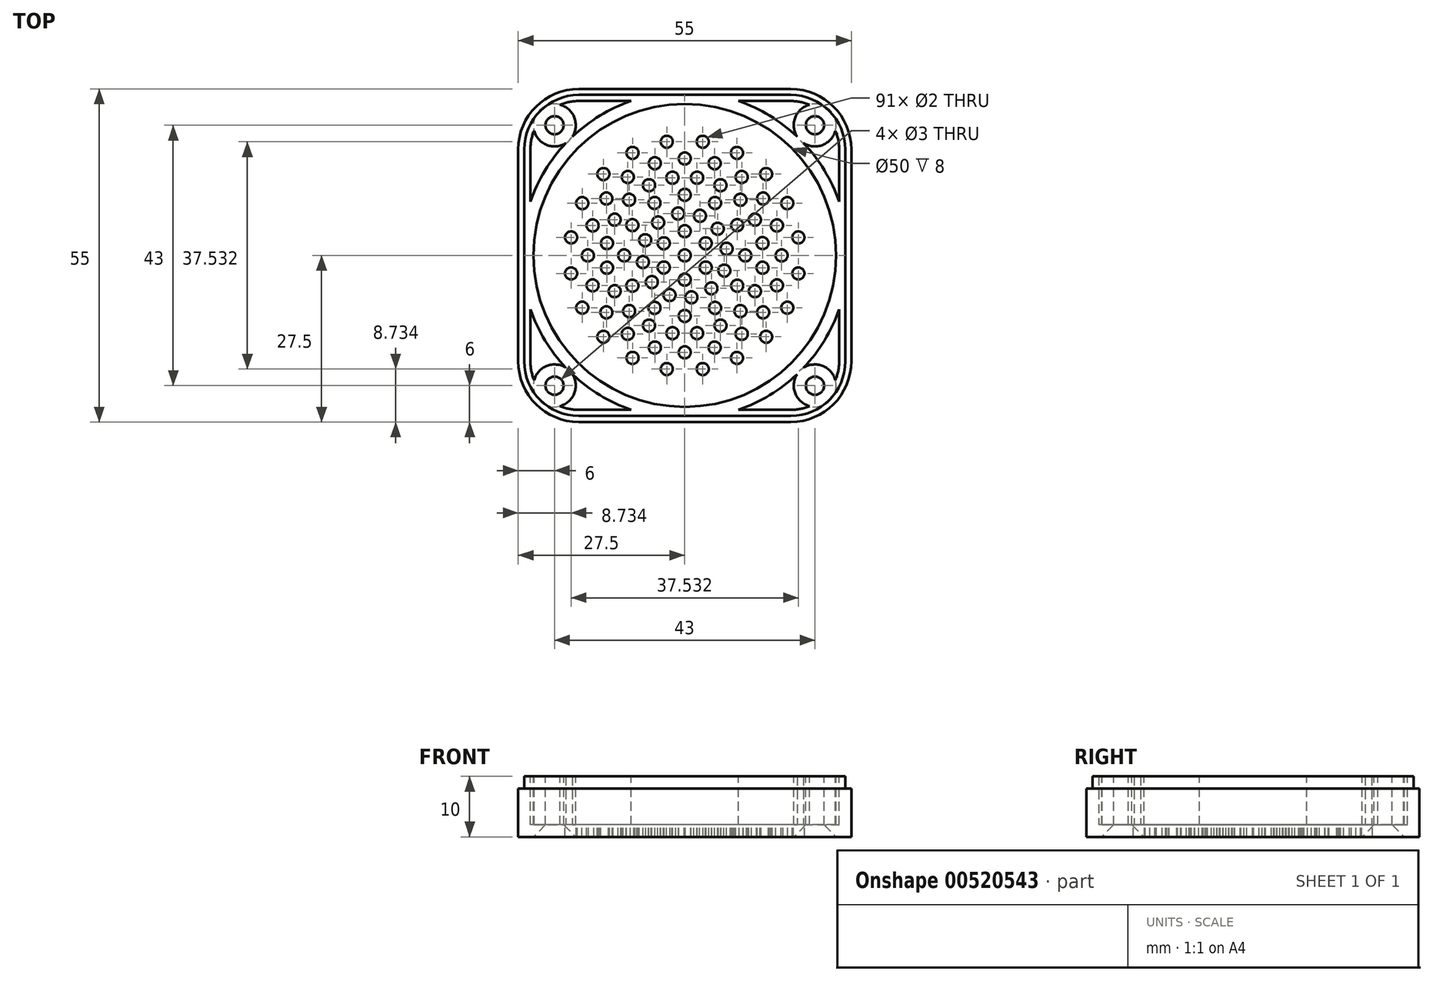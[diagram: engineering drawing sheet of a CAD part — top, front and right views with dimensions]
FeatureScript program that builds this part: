
annotation { "Feature Type Name" : "Feature", "Feature Type Description" : "" }
export const myFeature = defineFeature(function(context is Context, id is Id, definition is map)
    precondition{}
    {
        {
            var Q0;
            Q0=qCreatedBy(makeId("Top.planeOp"),FACE);
            var sketch = newSketch(context, id + "F0", { "sketchPlane" : qUnion([Q0])});
            skLineSegment(sketch, "E0.bottom", {"start": v(17.5, -27.5) * mm, "end": v(-17.5, -27.5) * mm});
            skLineSegment(sketch, "E0.top", {"start": v(17.5, 27.5) * mm, "end": v(-17.5, 27.5) * mm});
            skLineSegment(sketch, "E0.left", {"start": v(27.5, -17.5) * mm, "end": v(27.5, 17.5) * mm});
            skLineSegment(sketch, "E0.right", {"start": v(-27.5, -17.5) * mm, "end": v(-27.5, 17.5) * mm});
            skPoint(sketch, "E0.middle", {"position": v(0, 0) * mm});
            skPoint(sketch, "E1.visualSharp", {"position": v(-27.5, 27.5) * mm});
            skArc(sketch, "E1.filletArc", {"start": v(-17.5, 27.5) * mm, "mid": v(-24.57, 24.57) * mm, "end": v(-27.5, 17.5) * mm});
            skPoint(sketch, "E2.visualSharp", {"position": v(27.5, 27.5) * mm});
            skArc(sketch, "E2.filletArc", {"start": v(27.5, 17.5) * mm, "mid": v(24.57, 24.57) * mm, "end": v(17.5, 27.5) * mm});
            skPoint(sketch, "E3.visualSharp", {"position": v(27.5, -27.5) * mm});
            skArc(sketch, "E3.filletArc", {"start": v(17.5, -27.5) * mm, "mid": v(24.57, -24.57) * mm, "end": v(27.5, -17.5) * mm});
            skPoint(sketch, "E4.visualSharp", {"position": v(-27.5, -27.5) * mm});
            skArc(sketch, "E4.filletArc", {"start": v(-27.5, -17.5) * mm, "mid": v(-24.57, -24.57) * mm, "end": v(-17.5, -27.5) * mm});
            skSolve(sketch);
        }
        {
            var Q0;
            Q0=makeQuery(id+"F0.imprint","IMPRINT",FACE,{"disambiguationData":[TD([[makeQuery(id+"F0.imprint","IMPRINT",EDGE,{"derivedFrom":sQuery(id+"F0.wireOp",EDGE,"E0.bottom")}),-1.0]])]});
            extrude(context, id + "F1", {"entities" : qUnion([Q0]), "depth" : 10 * mm, "offsetDistance" : 25 * mm});
        }
        {
            var Q0;
            Q0=makeQuery(id+"F1.opExtrude","CAP_FACE",FACE,{"disambiguationData":[OSD([sQuery(id+"F0.wireOp",EDGE,"E0.bottom"),sQuery(id+"F0.wireOp",EDGE,"E0.top"),sQuery(id+"F0.wireOp",EDGE,"E0.left"),sQuery(id+"F0.wireOp",EDGE,"E0.right"),sQuery(id+"F0.wireOp",EDGE,"E1.filletArc"),sQuery(id+"F0.wireOp",EDGE,"E2.filletArc"),sQuery(id+"F0.wireOp",EDGE,"E3.filletArc"),sQuery(id+"F0.wireOp",EDGE,"E4.filletArc")])],"isStart":false});
            var sketch = newSketch(context, id + "F2", { "sketchPlane" : qUnion([Q0])});
            skCircle(sketch, "E5", {"center": v(-13.44, 13.44) * mm, "radius": 1 * mm});
            skCircle(sketch, "E6.1.0", {"center": v(-16.93, 8.63) * mm, "radius": 1 * mm});
            skCircle(sketch, "E6.2.0", {"center": v(-18.77, 2.97) * mm, "radius": 1 * mm});
            skCircle(sketch, "E6.3.0", {"center": v(-18.77, -2.97) * mm, "radius": 1 * mm});
            skCircle(sketch, "E6.4.0", {"center": v(-16.93, -8.63) * mm, "radius": 1 * mm});
            skCircle(sketch, "E6.5.0", {"center": v(-13.44, -13.44) * mm, "radius": 1 * mm});
            skCircle(sketch, "E6.6.0", {"center": v(-8.63, -16.93) * mm, "radius": 1 * mm});
            skCircle(sketch, "E6.7.0", {"center": v(-2.97, -18.77) * mm, "radius": 1 * mm});
            skCircle(sketch, "E6.8.0", {"center": v(2.97, -18.77) * mm, "radius": 1 * mm});
            skCircle(sketch, "E6.9.0", {"center": v(8.63, -16.93) * mm, "radius": 1 * mm});
            skCircle(sketch, "E6.10.0", {"center": v(13.44, -13.44) * mm, "radius": 1 * mm});
            skCircle(sketch, "E6.11.0", {"center": v(16.93, -8.63) * mm, "radius": 1 * mm});
            skCircle(sketch, "E6.12.0", {"center": v(18.77, -2.97) * mm, "radius": 1 * mm});
            skCircle(sketch, "E6.13.0", {"center": v(18.77, 2.97) * mm, "radius": 1 * mm});
            skCircle(sketch, "E6.14.0", {"center": v(16.93, 8.63) * mm, "radius": 1 * mm});
            skCircle(sketch, "E6.15.0", {"center": v(13.44, 13.44) * mm, "radius": 1 * mm});
            skCircle(sketch, "E6.16.0", {"center": v(8.63, 16.93) * mm, "radius": 1 * mm});
            skCircle(sketch, "E6.17.0", {"center": v(2.97, 18.77) * mm, "radius": 1 * mm});
            skCircle(sketch, "E6.18.0", {"center": v(-2.97, 18.77) * mm, "radius": 1 * mm});
            skCircle(sketch, "E6.19.0", {"center": v(-8.63, 16.93) * mm, "radius": 1 * mm});
            skPoint(sketch, "E6.center", {"position": v(0, 0) * mm});
            skCircle(sketch, "E7", {"center": v(-9.4, 12.94) * mm, "radius": 1 * mm});
            skCircle(sketch, "E8.1.0", {"center": v(-12.94, 9.4) * mm, "radius": 1 * mm});
            skCircle(sketch, "E8.2.0", {"center": v(-15.22, 4.94) * mm, "radius": 1 * mm});
            skCircle(sketch, "E8.3.0", {"center": v(-16, 0) * mm, "radius": 1 * mm});
            skCircle(sketch, "E8.4.0", {"center": v(-15.22, -4.94) * mm, "radius": 1 * mm});
            skCircle(sketch, "E8.5.0", {"center": v(-12.94, -9.4) * mm, "radius": 1 * mm});
            skCircle(sketch, "E8.6.0", {"center": v(-9.4, -12.94) * mm, "radius": 1 * mm});
            skCircle(sketch, "E8.7.0", {"center": v(-4.94, -15.22) * mm, "radius": 1 * mm});
            skCircle(sketch, "E8.8.0", {"center": v(0, -16) * mm, "radius": 1 * mm});
            skCircle(sketch, "E8.9.0", {"center": v(4.94, -15.22) * mm, "radius": 1 * mm});
            skCircle(sketch, "E8.10.0", {"center": v(9.4, -12.94) * mm, "radius": 1 * mm});
            skCircle(sketch, "E8.11.0", {"center": v(12.94, -9.4) * mm, "radius": 1 * mm});
            skCircle(sketch, "E8.12.0", {"center": v(15.22, -4.94) * mm, "radius": 1 * mm});
            skCircle(sketch, "E8.13.0", {"center": v(16, 0) * mm, "radius": 1 * mm});
            skCircle(sketch, "E8.14.0", {"center": v(15.22, 4.94) * mm, "radius": 1 * mm});
            skCircle(sketch, "E8.15.0", {"center": v(12.94, 9.4) * mm, "radius": 1 * mm});
            skCircle(sketch, "E8.16.0", {"center": v(9.4, 12.94) * mm, "radius": 1 * mm});
            skCircle(sketch, "E8.17.0", {"center": v(4.94, 15.22) * mm, "radius": 1 * mm});
            skCircle(sketch, "E8.18.0", {"center": v(0, 16) * mm, "radius": 1 * mm});
            skCircle(sketch, "E8.19.0", {"center": v(-4.94, 15.22) * mm, "radius": 1 * mm});
            skLineSegment(sketch, "E9", {"start": v(0, 29.56) * mm, "end": v(0, 0) * mm, "construction": true});
            skPoint(sketch, "E9.startSnap0", {"position": v(0, 27.5) * mm});
            skLineSegment(sketch, "E10", {"start": v(0, 0) * mm, "end": v(-5.19, 32.75) * mm, "construction": true});
            skCircle(sketch, "E11", {"center": v(-2.03, 12.84) * mm, "radius": 1 * mm});
            skCircle(sketch, "E12.1.0", {"center": v(-5.9, 11.58) * mm, "radius": 1 * mm});
            skCircle(sketch, "E12.2.0", {"center": v(-9.2, 9.2) * mm, "radius": 1 * mm});
            skCircle(sketch, "E12.3.0", {"center": v(-11.58, 5.9) * mm, "radius": 1 * mm});
            skCircle(sketch, "E12.4.0", {"center": v(-12.84, 2.03) * mm, "radius": 1 * mm});
            skCircle(sketch, "E12.5.0", {"center": v(-12.84, -2.03) * mm, "radius": 1 * mm});
            skCircle(sketch, "E12.6.0", {"center": v(-11.58, -5.9) * mm, "radius": 1 * mm});
            skCircle(sketch, "E12.7.0", {"center": v(-9.2, -9.2) * mm, "radius": 1 * mm});
            skCircle(sketch, "E12.8.0", {"center": v(-5.9, -11.58) * mm, "radius": 1 * mm});
            skCircle(sketch, "E12.9.0", {"center": v(-2.03, -12.84) * mm, "radius": 1 * mm});
            skCircle(sketch, "E12.10.0", {"center": v(2.03, -12.84) * mm, "radius": 1 * mm});
            skCircle(sketch, "E12.11.0", {"center": v(5.9, -11.58) * mm, "radius": 1 * mm});
            skCircle(sketch, "E12.12.0", {"center": v(9.2, -9.2) * mm, "radius": 1 * mm});
            skCircle(sketch, "E12.13.0", {"center": v(11.58, -5.9) * mm, "radius": 1 * mm});
            skCircle(sketch, "E12.14.0", {"center": v(12.84, -2.03) * mm, "radius": 1 * mm});
            skCircle(sketch, "E12.15.0", {"center": v(12.84, 2.03) * mm, "radius": 1 * mm});
            skCircle(sketch, "E12.16.0", {"center": v(11.58, 5.9) * mm, "radius": 1 * mm});
            skCircle(sketch, "E12.17.0", {"center": v(9.2, 9.2) * mm, "radius": 1 * mm});
            skCircle(sketch, "E12.18.0", {"center": v(5.9, 11.58) * mm, "radius": 1 * mm});
            skCircle(sketch, "E12.19.0", {"center": v(2.03, 12.84) * mm, "radius": 1 * mm});
            skCircle(sketch, "E13", {"center": v(0, 10) * mm, "radius": 1 * mm});
            skCircle(sketch, "E14.1.0", {"center": v(-5, 8.66) * mm, "radius": 1 * mm});
            skCircle(sketch, "E14.2.0", {"center": v(-8.66, 5) * mm, "radius": 1 * mm});
            skCircle(sketch, "E14.3.0", {"center": v(-10, 0) * mm, "radius": 1 * mm});
            skCircle(sketch, "E14.4.0", {"center": v(-8.66, -5) * mm, "radius": 1 * mm});
            skCircle(sketch, "E14.5.0", {"center": v(-5, -8.66) * mm, "radius": 1 * mm});
            skCircle(sketch, "E14.6.0", {"center": v(0, -10) * mm, "radius": 1 * mm});
            skCircle(sketch, "E14.7.0", {"center": v(5, -8.66) * mm, "radius": 1 * mm});
            skCircle(sketch, "E14.8.0", {"center": v(8.66, -5) * mm, "radius": 1 * mm});
            skCircle(sketch, "E14.9.0", {"center": v(10, 0) * mm, "radius": 1 * mm});
            skCircle(sketch, "E14.10.0", {"center": v(8.66, 5) * mm, "radius": 1 * mm});
            skCircle(sketch, "E14.11.0", {"center": v(5, 8.66) * mm, "radius": 1 * mm});
            skCircle(sketch, "E15", {"center": v(-1.1, 6.91) * mm, "radius": 1 * mm});
            skCircle(sketch, "E16.1.0", {"center": v(-4.4, 5.44) * mm, "radius": 1 * mm});
            skCircle(sketch, "E16.2.0", {"center": v(-6.54, 2.5) * mm, "radius": 1 * mm});
            skCircle(sketch, "E16.3.0", {"center": v(-6.91, -1.1) * mm, "radius": 1 * mm});
            skCircle(sketch, "E16.4.0", {"center": v(-5.44, -4.4) * mm, "radius": 1 * mm});
            skCircle(sketch, "E16.5.0", {"center": v(-2.5, -6.54) * mm, "radius": 1 * mm});
            skCircle(sketch, "E16.6.0", {"center": v(1.1, -6.91) * mm, "radius": 1 * mm});
            skCircle(sketch, "E16.7.0", {"center": v(4.4, -5.44) * mm, "radius": 1 * mm});
            skCircle(sketch, "E16.8.0", {"center": v(6.54, -2.5) * mm, "radius": 1 * mm});
            skCircle(sketch, "E16.9.0", {"center": v(6.91, 1.1) * mm, "radius": 1 * mm});
            skCircle(sketch, "E16.10.0", {"center": v(5.44, 4.4) * mm, "radius": 1 * mm});
            skCircle(sketch, "E16.11.0", {"center": v(2.5, 6.54) * mm, "radius": 1 * mm});
            skCircle(sketch, "E17", {"center": v(0, 4) * mm, "radius": 1 * mm});
            skCircle(sketch, "E18", {"center": v(0, 0) * mm, "radius": 1 * mm});
            skCircle(sketch, "E19.1.0", {"center": v(-3.46, 2) * mm, "radius": 1 * mm});
            skCircle(sketch, "E19.2.0", {"center": v(-3.46, -2) * mm, "radius": 1 * mm});
            skCircle(sketch, "E19.3.0", {"center": v(0, -4) * mm, "radius": 1 * mm});
            skCircle(sketch, "E19.4.0", {"center": v(3.46, -2) * mm, "radius": 1 * mm});
            skCircle(sketch, "E19.5.0", {"center": v(3.46, 2) * mm, "radius": 1 * mm});
            skSolve(sketch);
        }
        {
            var Q0;
            Q0=makeQuery(id+"F2.imprint","IMPRINT",FACE,{"disambiguationData":[TD([[makeQuery(id+"F2.imprint","IMPRINT",EDGE,{"derivedFrom":sQuery(id+"F2.wireOp",EDGE,"E14.10.0")}),1.0]])]});
            var Q1;
            Q1=makeQuery(id+"F2.imprint","IMPRINT",FACE,{"disambiguationData":[TD([[makeQuery(id+"F2.imprint","IMPRINT",EDGE,{"derivedFrom":sQuery(id+"F2.wireOp",EDGE,"E12.7.0")}),1.0]])]});
            var Q2;
            Q2=makeQuery(id+"F2.imprint","IMPRINT",FACE,{"disambiguationData":[TD([[makeQuery(id+"F2.imprint","IMPRINT",EDGE,{"derivedFrom":sQuery(id+"F2.wireOp",EDGE,"E12.14.0")}),1.0]])]});
            var Q3;
            Q3=makeQuery(id+"F2.imprint","IMPRINT",FACE,{"disambiguationData":[TD([[makeQuery(id+"F2.imprint","IMPRINT",EDGE,{"derivedFrom":sQuery(id+"F2.wireOp",EDGE,"E6.10.0")}),1.0]])]});
            var Q4;
            Q4=makeQuery(id+"F2.imprint","IMPRINT",FACE,{"disambiguationData":[TD([[makeQuery(id+"F2.imprint","IMPRINT",EDGE,{"derivedFrom":sQuery(id+"F2.wireOp",EDGE,"E12.1.0")}),1.0]])]});
            var Q5;
            Q5=makeQuery(id+"F2.imprint","IMPRINT",FACE,{"disambiguationData":[TD([[makeQuery(id+"F2.imprint","IMPRINT",EDGE,{"derivedFrom":sQuery(id+"F2.wireOp",EDGE,"E8.5.0")}),1.0]])]});
            var Q6;
            Q6=makeQuery(id+"F2.imprint","IMPRINT",FACE,{"disambiguationData":[TD([[makeQuery(id+"F2.imprint","IMPRINT",EDGE,{"derivedFrom":sQuery(id+"F2.wireOp",EDGE,"E6.1.0")}),1.0]])]});
            var Q7;
            Q7=makeQuery(id+"F2.imprint","IMPRINT",FACE,{"disambiguationData":[TD([[makeQuery(id+"F2.imprint","IMPRINT",EDGE,{"derivedFrom":sQuery(id+"F2.wireOp",EDGE,"E6.11.0")}),1.0]])]});
            var Q8;
            Q8=makeQuery(id+"F2.imprint","IMPRINT",FACE,{"disambiguationData":[TD([[makeQuery(id+"F2.imprint","IMPRINT",EDGE,{"derivedFrom":sQuery(id+"F2.wireOp",EDGE,"E12.17.0")}),1.0]])]});
            var Q9;
            Q9=makeQuery(id+"F2.imprint","IMPRINT",FACE,{"disambiguationData":[TD([[makeQuery(id+"F2.imprint","IMPRINT",EDGE,{"derivedFrom":sQuery(id+"F2.wireOp",EDGE,"E6.12.0")}),1.0]])]});
            var Q10;
            Q10=makeQuery(id+"F2.imprint","IMPRINT",FACE,{"disambiguationData":[TD([[makeQuery(id+"F2.imprint","IMPRINT",EDGE,{"derivedFrom":sQuery(id+"F2.wireOp",EDGE,"E16.7.0")}),1.0]])]});
            var Q11;
            Q11=makeQuery(id+"F2.imprint","IMPRINT",FACE,{"disambiguationData":[TD([[makeQuery(id+"F2.imprint","IMPRINT",EDGE,{"derivedFrom":sQuery(id+"F2.wireOp",EDGE,"E8.2.0")}),1.0]])]});
            var Q12;
            Q12=makeQuery(id+"F2.imprint","IMPRINT",FACE,{"disambiguationData":[TD([[makeQuery(id+"F2.imprint","IMPRINT",EDGE,{"derivedFrom":sQuery(id+"F2.wireOp",EDGE,"E8.18.0")}),1.0]])]});
            var Q13;
            Q13=makeQuery(id+"F2.imprint","IMPRINT",FACE,{"disambiguationData":[TD([[makeQuery(id+"F2.imprint","IMPRINT",EDGE,{"derivedFrom":sQuery(id+"F2.wireOp",EDGE,"E19.1.0")}),1.0]])]});
            var Q14;
            Q14=makeQuery(id+"F2.imprint","IMPRINT",FACE,{"disambiguationData":[TD([[makeQuery(id+"F2.imprint","IMPRINT",EDGE,{"derivedFrom":sQuery(id+"F2.wireOp",EDGE,"E8.12.0")}),1.0]])]});
            var Q15;
            Q15=makeQuery(id+"F2.imprint","IMPRINT",FACE,{"disambiguationData":[TD([[makeQuery(id+"F2.imprint","IMPRINT",EDGE,{"derivedFrom":sQuery(id+"F2.wireOp",EDGE,"E19.4.0")}),1.0]])]});
            var Q16;
            Q16=makeQuery(id+"F2.imprint","IMPRINT",FACE,{"disambiguationData":[TD([[makeQuery(id+"F2.imprint","IMPRINT",EDGE,{"derivedFrom":sQuery(id+"F2.wireOp",EDGE,"E6.2.0")}),1.0]])]});
            var Q17;
            Q17=makeQuery(id+"F2.imprint","IMPRINT",FACE,{"disambiguationData":[TD([[makeQuery(id+"F2.imprint","IMPRINT",EDGE,{"derivedFrom":sQuery(id+"F2.wireOp",EDGE,"E14.3.0")}),1.0]])]});
            var Q18;
            Q18=makeQuery(id+"F2.imprint","IMPRINT",FACE,{"disambiguationData":[TD([[makeQuery(id+"F2.imprint","IMPRINT",EDGE,{"derivedFrom":sQuery(id+"F2.wireOp",EDGE,"E8.15.0")}),1.0]])]});
            var Q19;
            Q19=makeQuery(id+"F2.imprint","IMPRINT",FACE,{"disambiguationData":[TD([[makeQuery(id+"F2.imprint","IMPRINT",EDGE,{"derivedFrom":sQuery(id+"F2.wireOp",EDGE,"E6.3.0")}),1.0]])]});
            var Q20;
            Q20=makeQuery(id+"F2.imprint","IMPRINT",FACE,{"disambiguationData":[TD([[makeQuery(id+"F2.imprint","IMPRINT",EDGE,{"derivedFrom":sQuery(id+"F2.wireOp",EDGE,"E6.4.0")}),1.0]])]});
            var Q21;
            Q21=makeQuery(id+"F2.imprint","IMPRINT",FACE,{"disambiguationData":[TD([[makeQuery(id+"F2.imprint","IMPRINT",EDGE,{"derivedFrom":sQuery(id+"F2.wireOp",EDGE,"E13")}),1.0]])]});
            var Q22;
            Q22=makeQuery(id+"F2.imprint","IMPRINT",FACE,{"disambiguationData":[TD([[makeQuery(id+"F2.imprint","IMPRINT",EDGE,{"derivedFrom":sQuery(id+"F2.wireOp",EDGE,"E6.5.0")}),1.0]])]});
            var Q23;
            Q23=makeQuery(id+"F2.imprint","IMPRINT",FACE,{"disambiguationData":[TD([[makeQuery(id+"F2.imprint","IMPRINT",EDGE,{"derivedFrom":sQuery(id+"F2.wireOp",EDGE,"E6.8.0")}),1.0]])]});
            var Q24;
            Q24=makeQuery(id+"F2.imprint","IMPRINT",FACE,{"disambiguationData":[TD([[makeQuery(id+"F2.imprint","IMPRINT",EDGE,{"derivedFrom":sQuery(id+"F2.wireOp",EDGE,"E6.7.0")}),1.0]])]});
            var Q25;
            Q25=makeQuery(id+"F2.imprint","IMPRINT",FACE,{"disambiguationData":[TD([[makeQuery(id+"F2.imprint","IMPRINT",EDGE,{"derivedFrom":sQuery(id+"F2.wireOp",EDGE,"E6.6.0")}),1.0]])]});
            var Q26;
            Q26=makeQuery(id+"F2.imprint","IMPRINT",FACE,{"disambiguationData":[TD([[makeQuery(id+"F2.imprint","IMPRINT",EDGE,{"derivedFrom":sQuery(id+"F2.wireOp",EDGE,"E6.9.0")}),1.0]])]});
            var Q27;
            Q27=makeQuery(id+"F2.imprint","IMPRINT",FACE,{"disambiguationData":[TD([[makeQuery(id+"F2.imprint","IMPRINT",EDGE,{"derivedFrom":sQuery(id+"F2.wireOp",EDGE,"E16.1.0")}),1.0]])]});
            var Q28;
            Q28=makeQuery(id+"F2.imprint","IMPRINT",FACE,{"disambiguationData":[TD([[makeQuery(id+"F2.imprint","IMPRINT",EDGE,{"derivedFrom":sQuery(id+"F2.wireOp",EDGE,"E16.8.0")}),1.0]])]});
            var Q29;
            Q29=makeQuery(id+"F2.imprint","IMPRINT",FACE,{"disambiguationData":[TD([[makeQuery(id+"F2.imprint","IMPRINT",EDGE,{"derivedFrom":sQuery(id+"F2.wireOp",EDGE,"E8.11.0")}),1.0]])]});
            var Q30;
            Q30=makeQuery(id+"F2.imprint","IMPRINT",FACE,{"disambiguationData":[TD([[makeQuery(id+"F2.imprint","IMPRINT",EDGE,{"derivedFrom":sQuery(id+"F2.wireOp",EDGE,"E14.4.0")}),1.0]])]});
            var Q31;
            Q31=makeQuery(id+"F2.imprint","IMPRINT",FACE,{"disambiguationData":[TD([[makeQuery(id+"F2.imprint","IMPRINT",EDGE,{"derivedFrom":sQuery(id+"F2.wireOp",EDGE,"E16.4.0")}),1.0]])]});
            var Q32;
            Q32=makeQuery(id+"F2.imprint","IMPRINT",FACE,{"disambiguationData":[TD([[makeQuery(id+"F2.imprint","IMPRINT",EDGE,{"derivedFrom":sQuery(id+"F2.wireOp",EDGE,"E16.11.0")}),1.0]])]});
            var Q33;
            Q33=makeQuery(id+"F2.imprint","IMPRINT",FACE,{"disambiguationData":[TD([[makeQuery(id+"F2.imprint","IMPRINT",EDGE,{"derivedFrom":sQuery(id+"F2.wireOp",EDGE,"E6.19.0")}),1.0]])]});
            var Q34;
            Q34=makeQuery(id+"F2.imprint","IMPRINT",FACE,{"disambiguationData":[TD([[makeQuery(id+"F2.imprint","IMPRINT",EDGE,{"derivedFrom":sQuery(id+"F2.wireOp",EDGE,"E14.7.0")}),1.0]])]});
            var Q35;
            Q35=makeQuery(id+"F2.imprint","IMPRINT",FACE,{"disambiguationData":[TD([[makeQuery(id+"F2.imprint","IMPRINT",EDGE,{"derivedFrom":sQuery(id+"F2.wireOp",EDGE,"E12.11.0")}),1.0]])]});
            var Q36;
            Q36=makeQuery(id+"F2.imprint","IMPRINT",FACE,{"disambiguationData":[TD([[makeQuery(id+"F2.imprint","IMPRINT",EDGE,{"derivedFrom":sQuery(id+"F2.wireOp",EDGE,"E6.16.0")}),1.0]])]});
            var Q37;
            Q37=makeQuery(id+"F2.imprint","IMPRINT",FACE,{"disambiguationData":[TD([[makeQuery(id+"F2.imprint","IMPRINT",EDGE,{"derivedFrom":sQuery(id+"F2.wireOp",EDGE,"E12.18.0")}),1.0]])]});
            var Q38;
            Q38=makeQuery(id+"F2.imprint","IMPRINT",FACE,{"disambiguationData":[TD([[makeQuery(id+"F2.imprint","IMPRINT",EDGE,{"derivedFrom":sQuery(id+"F2.wireOp",EDGE,"E16.2.0")}),1.0]])]});
            var Q39;
            Q39=makeQuery(id+"F2.imprint","IMPRINT",FACE,{"disambiguationData":[TD([[makeQuery(id+"F2.imprint","IMPRINT",EDGE,{"derivedFrom":sQuery(id+"F2.wireOp",EDGE,"E12.8.0")}),1.0]])]});
            var Q40;
            Q40=makeQuery(id+"F2.imprint","IMPRINT",FACE,{"disambiguationData":[TD([[makeQuery(id+"F2.imprint","IMPRINT",EDGE,{"derivedFrom":sQuery(id+"F2.wireOp",EDGE,"E19.2.0")}),1.0]])]});
            var Q41;
            Q41=makeQuery(id+"F2.imprint","IMPRINT",FACE,{"disambiguationData":[TD([[makeQuery(id+"F2.imprint","IMPRINT",EDGE,{"derivedFrom":sQuery(id+"F2.wireOp",EDGE,"E12.6.0")}),1.0]])]});
            var Q42;
            Q42=makeQuery(id+"F2.imprint","IMPRINT",FACE,{"disambiguationData":[TD([[makeQuery(id+"F2.imprint","IMPRINT",EDGE,{"derivedFrom":sQuery(id+"F2.wireOp",EDGE,"E12.13.0")}),1.0]])]});
            var Q43;
            Q43=makeQuery(id+"F2.imprint","IMPRINT",FACE,{"disambiguationData":[TD([[makeQuery(id+"F2.imprint","IMPRINT",EDGE,{"derivedFrom":sQuery(id+"F2.wireOp",EDGE,"E14.11.0")}),1.0]])]});
            var Q44;
            Q44=makeQuery(id+"F2.imprint","IMPRINT",FACE,{"disambiguationData":[TD([[makeQuery(id+"F2.imprint","IMPRINT",EDGE,{"derivedFrom":sQuery(id+"F2.wireOp",EDGE,"E8.8.0")}),1.0]])]});
            var Q45;
            Q45=makeQuery(id+"F2.imprint","IMPRINT",FACE,{"disambiguationData":[TD([[makeQuery(id+"F2.imprint","IMPRINT",EDGE,{"derivedFrom":sQuery(id+"F2.wireOp",EDGE,"E14.9.0")}),1.0]])]});
            var Q46;
            Q46=makeQuery(id+"F2.imprint","IMPRINT",FACE,{"disambiguationData":[TD([[makeQuery(id+"F2.imprint","IMPRINT",EDGE,{"derivedFrom":sQuery(id+"F2.wireOp",EDGE,"E14.2.0")}),1.0]])]});
            var Q47;
            Q47=makeQuery(id+"F2.imprint","IMPRINT",FACE,{"disambiguationData":[TD([[makeQuery(id+"F2.imprint","IMPRINT",EDGE,{"derivedFrom":sQuery(id+"F2.wireOp",EDGE,"E12.4.0")}),1.0]])]});
            var Q48;
            Q48=makeQuery(id+"F2.imprint","IMPRINT",FACE,{"disambiguationData":[TD([[makeQuery(id+"F2.imprint","IMPRINT",EDGE,{"derivedFrom":sQuery(id+"F2.wireOp",EDGE,"E12.15.0")}),1.0]])]});
            var Q49;
            Q49=makeQuery(id+"F2.imprint","IMPRINT",FACE,{"disambiguationData":[TD([[makeQuery(id+"F2.imprint","IMPRINT",EDGE,{"derivedFrom":sQuery(id+"F2.wireOp",EDGE,"E8.19.0")}),1.0]])]});
            var Q50;
            Q50=makeQuery(id+"F2.imprint","IMPRINT",FACE,{"disambiguationData":[TD([[makeQuery(id+"F2.imprint","IMPRINT",EDGE,{"derivedFrom":sQuery(id+"F2.wireOp",EDGE,"E16.6.0")}),1.0]])]});
            var Q51;
            Q51=makeQuery(id+"F2.imprint","IMPRINT",FACE,{"disambiguationData":[TD([[makeQuery(id+"F2.imprint","IMPRINT",EDGE,{"derivedFrom":sQuery(id+"F2.wireOp",EDGE,"E12.2.0")}),1.0]])]});
            var Q52;
            Q52=makeQuery(id+"F2.imprint","IMPRINT",FACE,{"disambiguationData":[TD([[makeQuery(id+"F2.imprint","IMPRINT",EDGE,{"derivedFrom":sQuery(id+"F2.wireOp",EDGE,"E8.6.0")}),1.0]])]});
            var Q53;
            Q53=makeQuery(id+"F2.imprint","IMPRINT",FACE,{"disambiguationData":[TD([[makeQuery(id+"F2.imprint","IMPRINT",EDGE,{"derivedFrom":sQuery(id+"F2.wireOp",EDGE,"E8.3.0")}),1.0]])]});
            var Q54;
            Q54=makeQuery(id+"F2.imprint","IMPRINT",FACE,{"disambiguationData":[TD([[makeQuery(id+"F2.imprint","IMPRINT",EDGE,{"derivedFrom":sQuery(id+"F2.wireOp",EDGE,"E8.1.0")}),1.0]])]});
            var Q55;
            Q55=makeQuery(id+"F2.imprint","IMPRINT",FACE,{"disambiguationData":[TD([[makeQuery(id+"F2.imprint","IMPRINT",EDGE,{"derivedFrom":sQuery(id+"F2.wireOp",EDGE,"E8.17.0")}),1.0]])]});
            var Q56;
            Q56=makeQuery(id+"F2.imprint","IMPRINT",FACE,{"disambiguationData":[TD([[makeQuery(id+"F2.imprint","IMPRINT",EDGE,{"derivedFrom":sQuery(id+"F2.wireOp",EDGE,"E8.10.0")}),1.0]])]});
            var Q57;
            Q57=makeQuery(id+"F2.imprint","IMPRINT",FACE,{"disambiguationData":[TD([[makeQuery(id+"F2.imprint","IMPRINT",EDGE,{"derivedFrom":sQuery(id+"F2.wireOp",EDGE,"E8.13.0")}),1.0]])]});
            var Q58;
            Q58=makeQuery(id+"F2.imprint","IMPRINT",FACE,{"disambiguationData":[TD([[makeQuery(id+"F2.imprint","IMPRINT",EDGE,{"derivedFrom":sQuery(id+"F2.wireOp",EDGE,"E6.17.0")}),1.0]])]});
            var Q59;
            Q59=makeQuery(id+"F2.imprint","IMPRINT",FACE,{"disambiguationData":[TD([[makeQuery(id+"F2.imprint","IMPRINT",EDGE,{"derivedFrom":sQuery(id+"F2.wireOp",EDGE,"E16.9.0")}),1.0]])]});
            var Q60;
            Q60=makeQuery(id+"F2.imprint","IMPRINT",FACE,{"disambiguationData":[TD([[makeQuery(id+"F2.imprint","IMPRINT",EDGE,{"derivedFrom":sQuery(id+"F2.wireOp",EDGE,"E8.7.0")}),1.0]])]});
            var Q61;
            Q61=makeQuery(id+"F2.imprint","IMPRINT",FACE,{"disambiguationData":[TD([[makeQuery(id+"F2.imprint","IMPRINT",EDGE,{"derivedFrom":sQuery(id+"F2.wireOp",EDGE,"E12.3.0")}),1.0]])]});
            var Q62;
            Q62=makeQuery(id+"F2.imprint","IMPRINT",FACE,{"disambiguationData":[TD([[makeQuery(id+"F2.imprint","IMPRINT",EDGE,{"derivedFrom":sQuery(id+"F2.wireOp",EDGE,"E14.5.0")}),1.0]])]});
            var Q63;
            Q63=makeQuery(id+"F2.imprint","IMPRINT",FACE,{"disambiguationData":[TD([[makeQuery(id+"F2.imprint","IMPRINT",EDGE,{"derivedFrom":sQuery(id+"F2.wireOp",EDGE,"E12.9.0")}),1.0]])]});
            var Q64;
            Q64=makeQuery(id+"F2.imprint","IMPRINT",FACE,{"disambiguationData":[TD([[makeQuery(id+"F2.imprint","IMPRINT",EDGE,{"derivedFrom":sQuery(id+"F2.wireOp",EDGE,"E12.19.0")}),1.0]])]});
            var Q65;
            Q65=makeQuery(id+"F2.imprint","IMPRINT",FACE,{"disambiguationData":[TD([[makeQuery(id+"F2.imprint","IMPRINT",EDGE,{"derivedFrom":sQuery(id+"F2.wireOp",EDGE,"E16.3.0")}),1.0]])]});
            var Q66;
            Q66=makeQuery(id+"F2.imprint","IMPRINT",FACE,{"disambiguationData":[TD([[makeQuery(id+"F2.imprint","IMPRINT",EDGE,{"derivedFrom":sQuery(id+"F2.wireOp",EDGE,"E5")}),1.0]])]});
            var Q67;
            Q67=makeQuery(id+"F2.imprint","IMPRINT",FACE,{"disambiguationData":[TD([[makeQuery(id+"F2.imprint","IMPRINT",EDGE,{"derivedFrom":sQuery(id+"F2.wireOp",EDGE,"E6.14.0")}),1.0]])]});
            var Q68;
            Q68=makeQuery(id+"F2.imprint","IMPRINT",FACE,{"disambiguationData":[TD([[makeQuery(id+"F2.imprint","IMPRINT",EDGE,{"derivedFrom":sQuery(id+"F2.wireOp",EDGE,"E6.13.0")}),1.0]])]});
            var Q69;
            Q69=makeQuery(id+"F2.imprint","IMPRINT",FACE,{"disambiguationData":[TD([[makeQuery(id+"F2.imprint","IMPRINT",EDGE,{"derivedFrom":sQuery(id+"F2.wireOp",EDGE,"E12.10.0")}),1.0]])]});
            var Q70;
            Q70=makeQuery(id+"F2.imprint","IMPRINT",FACE,{"disambiguationData":[TD([[makeQuery(id+"F2.imprint","IMPRINT",EDGE,{"derivedFrom":sQuery(id+"F2.wireOp",EDGE,"E6.15.0")}),1.0]])]});
            var Q71;
            Q71=makeQuery(id+"F2.imprint","IMPRINT",FACE,{"disambiguationData":[TD([[makeQuery(id+"F2.imprint","IMPRINT",EDGE,{"derivedFrom":sQuery(id+"F2.wireOp",EDGE,"E14.6.0")}),1.0]])]});
            var Q72;
            Q72=makeQuery(id+"F2.imprint","IMPRINT",FACE,{"disambiguationData":[TD([[makeQuery(id+"F2.imprint","IMPRINT",EDGE,{"derivedFrom":sQuery(id+"F2.wireOp",EDGE,"E16.10.0")}),1.0]])]});
            var Q73;
            Q73=makeQuery(id+"F2.imprint","IMPRINT",FACE,{"disambiguationData":[TD([[makeQuery(id+"F2.imprint","IMPRINT",EDGE,{"derivedFrom":sQuery(id+"F2.wireOp",EDGE,"E6.18.0")}),1.0]])]});
            var Q74;
            Q74=makeQuery(id+"F2.imprint","IMPRINT",FACE,{"disambiguationData":[TD([[makeQuery(id+"F2.imprint","IMPRINT",EDGE,{"derivedFrom":sQuery(id+"F2.wireOp",EDGE,"E8.14.0")}),1.0]])]});
            var Q75;
            Q75=makeQuery(id+"F2.imprint","IMPRINT",FACE,{"disambiguationData":[TD([[makeQuery(id+"F2.imprint","IMPRINT",EDGE,{"derivedFrom":sQuery(id+"F2.wireOp",EDGE,"E19.3.0")}),1.0]])]});
            var Q76;
            Q76=makeQuery(id+"F2.imprint","IMPRINT",FACE,{"disambiguationData":[TD([[makeQuery(id+"F2.imprint","IMPRINT",EDGE,{"derivedFrom":sQuery(id+"F2.wireOp",EDGE,"E8.4.0")}),1.0]])]});
            var Q77;
            Q77=makeQuery(id+"F2.imprint","IMPRINT",FACE,{"disambiguationData":[TD([[makeQuery(id+"F2.imprint","IMPRINT",EDGE,{"derivedFrom":sQuery(id+"F2.wireOp",EDGE,"E11")}),1.0]])]});
            var Q78;
            Q78=makeQuery(id+"F2.imprint","IMPRINT",FACE,{"disambiguationData":[TD([[makeQuery(id+"F2.imprint","IMPRINT",EDGE,{"derivedFrom":sQuery(id+"F2.wireOp",EDGE,"E15")}),1.0]])]});
            var Q79;
            Q79=makeQuery(id+"F2.imprint","IMPRINT",FACE,{"disambiguationData":[TD([[makeQuery(id+"F2.imprint","IMPRINT",EDGE,{"derivedFrom":sQuery(id+"F2.wireOp",EDGE,"E12.16.0")}),1.0]])]});
            var Q80;
            Q80=makeQuery(id+"F2.imprint","IMPRINT",FACE,{"disambiguationData":[TD([[makeQuery(id+"F2.imprint","IMPRINT",EDGE,{"derivedFrom":sQuery(id+"F2.wireOp",EDGE,"E19.5.0")}),1.0]])]});
            var Q81;
            Q81=makeQuery(id+"F2.imprint","IMPRINT",FACE,{"disambiguationData":[TD([[makeQuery(id+"F2.imprint","IMPRINT",EDGE,{"derivedFrom":sQuery(id+"F2.wireOp",EDGE,"E8.16.0")}),1.0]])]});
            var Q82;
            Q82=makeQuery(id+"F2.imprint","IMPRINT",FACE,{"disambiguationData":[TD([[makeQuery(id+"F2.imprint","IMPRINT",EDGE,{"derivedFrom":sQuery(id+"F2.wireOp",EDGE,"E8.9.0")}),1.0]])]});
            var Q83;
            Q83=makeQuery(id+"F2.imprint","IMPRINT",FACE,{"disambiguationData":[TD([[makeQuery(id+"F2.imprint","IMPRINT",EDGE,{"derivedFrom":sQuery(id+"F2.wireOp",EDGE,"E7")}),1.0]])]});
            var Q84;
            Q84=makeQuery(id+"F2.imprint","IMPRINT",FACE,{"disambiguationData":[TD([[makeQuery(id+"F2.imprint","IMPRINT",EDGE,{"derivedFrom":sQuery(id+"F2.wireOp",EDGE,"E16.5.0")}),1.0]])]});
            var Q85;
            Q85=makeQuery(id+"F2.imprint","IMPRINT",FACE,{"disambiguationData":[TD([[makeQuery(id+"F2.imprint","IMPRINT",EDGE,{"derivedFrom":sQuery(id+"F2.wireOp",EDGE,"E17")}),1.0]])]});
            var Q86;
            Q86=makeQuery(id+"F2.imprint","IMPRINT",FACE,{"disambiguationData":[TD([[makeQuery(id+"F2.imprint","IMPRINT",EDGE,{"derivedFrom":sQuery(id+"F2.wireOp",EDGE,"E14.1.0")}),1.0]])]});
            var Q87;
            Q87=makeQuery(id+"F2.imprint","IMPRINT",FACE,{"disambiguationData":[TD([[makeQuery(id+"F2.imprint","IMPRINT",EDGE,{"derivedFrom":sQuery(id+"F2.wireOp",EDGE,"E14.8.0")}),1.0]])]});
            var Q88;
            Q88=makeQuery(id+"F2.imprint","IMPRINT",FACE,{"disambiguationData":[TD([[makeQuery(id+"F2.imprint","IMPRINT",EDGE,{"derivedFrom":sQuery(id+"F2.wireOp",EDGE,"E12.12.0")}),1.0]])]});
            var Q89;
            Q89=makeQuery(id+"F2.imprint","IMPRINT",FACE,{"disambiguationData":[TD([[makeQuery(id+"F2.imprint","IMPRINT",EDGE,{"derivedFrom":sQuery(id+"F2.wireOp",EDGE,"E12.5.0")}),1.0]])]});
            var Q90;
            Q90=makeQuery(id+"F2.imprint","IMPRINT",FACE,{"disambiguationData":[TD([[makeQuery(id+"F2.imprint","IMPRINT",EDGE,{"derivedFrom":sQuery(id+"F2.wireOp",EDGE,"E18")}),1.0]])]});
            extrude(context, id + "F3", {"entities" : qUnion([Q0, Q1, Q2, Q3, Q4, Q5, Q6, Q7, Q8, Q9, Q10, Q11, Q12, Q13, Q14, Q15, Q16, Q17, Q18, Q19, Q20, Q21, Q22, Q23, Q24, Q25, Q26, Q27, Q28, Q29, Q30, Q31, Q32, Q33, Q34, Q35, Q36, Q37, Q38, Q39, Q40, Q41, Q42, Q43, Q44, Q45, Q46, Q47, Q48, Q49, Q50, Q51, Q52, Q53, Q54, Q55, Q56, Q57, Q58, Q59, Q60, Q61, Q62, Q63, Q64, Q65, Q66, Q67, Q68, Q69, Q70, Q71, Q72, Q73, Q74, Q75, Q76, Q77, Q78, Q79, Q80, Q81, Q82, Q83, Q84, Q85, Q86, Q87, Q88, Q89, Q90]), "operationType" : NewBodyOperationType.REMOVE, "endBound" : BoundingType.THROUGH_ALL, "oppositeDirection" : true, "depth" : 25 * mm, "offsetDistance" : 25 * mm});
        }
        {
            var Q0;
            Q0=makeQuery(id+"F1.opExtrude","CAP_FACE",FACE,{"disambiguationData":[OSD([sQuery(id+"F0.wireOp",EDGE,"E0.bottom"),sQuery(id+"F0.wireOp",EDGE,"E0.top"),sQuery(id+"F0.wireOp",EDGE,"E0.left"),sQuery(id+"F0.wireOp",EDGE,"E0.right"),sQuery(id+"F0.wireOp",EDGE,"E1.filletArc"),sQuery(id+"F0.wireOp",EDGE,"E2.filletArc"),sQuery(id+"F0.wireOp",EDGE,"E3.filletArc"),sQuery(id+"F0.wireOp",EDGE,"E4.filletArc")])],"isStart":false});
            var sketch = newSketch(context, id + "F4", { "sketchPlane" : qUnion([Q0])});
            skCircle(sketch, "E20", {"center": v(0, 0) * mm, "radius": 25 * mm});
            skSolve(sketch);
        }
        {
            var Q0;
            Q0 = qSketchRegion(id + "F4", true);
            extrude(context, id + "F5", {"entities" : qUnion([Q0]), "operationType" : NewBodyOperationType.REMOVE, "oppositeDirection" : true, "depth" : 8 * mm, "offsetDistance" : 25 * mm});
        }
        {
            var Q0;
            Q0=makeQuery(id+"F1.opExtrude","CAP_FACE",FACE,{"disambiguationData":[OSD([sQuery(id+"F0.wireOp",EDGE,"E0.bottom"),sQuery(id+"F0.wireOp",EDGE,"E0.top"),sQuery(id+"F0.wireOp",EDGE,"E0.left"),sQuery(id+"F0.wireOp",EDGE,"E0.right"),sQuery(id+"F0.wireOp",EDGE,"E1.filletArc"),sQuery(id+"F0.wireOp",EDGE,"E2.filletArc"),sQuery(id+"F0.wireOp",EDGE,"E3.filletArc"),sQuery(id+"F0.wireOp",EDGE,"E4.filletArc")])],"isStart":false});
            var sketch = newSketch(context, id + "F6", { "sketchPlane" : qUnion([Q0])});
            skLineSegment(sketch, "E21.bottom", {"start": v(21.5, -21.5) * mm, "end": v(-21.5, -21.5) * mm, "construction": true});
            skLineSegment(sketch, "E21.top", {"start": v(21.5, 21.5) * mm, "end": v(-21.5, 21.5) * mm, "construction": true});
            skLineSegment(sketch, "E21.left", {"start": v(21.5, -21.5) * mm, "end": v(21.5, 21.5) * mm, "construction": true});
            skLineSegment(sketch, "E21.right", {"start": v(-21.5, -21.5) * mm, "end": v(-21.5, 21.5) * mm, "construction": true});
            skPoint(sketch, "E21.middle", {"position": v(0, 0) * mm});
            skCircle(sketch, "E22", {"center": v(-21.5, 21.5) * mm, "radius": 1.5 * mm});
            skCircle(sketch, "E23", {"center": v(21.5, 21.5) * mm, "radius": 1.5 * mm});
            skCircle(sketch, "E24", {"center": v(21.5, -21.5) * mm, "radius": 1.5 * mm});
            skCircle(sketch, "E25", {"center": v(-21.5, -21.5) * mm, "radius": 1.5 * mm});
            skSolve(sketch);
        }
        {
            var Q0;
            Q0=makeQuery(id+"F6.imprint","IMPRINT",FACE,{"disambiguationData":[TD([[makeQuery(id+"F6.imprint","IMPRINT",EDGE,{"derivedFrom":sQuery(id+"F6.wireOp",EDGE,"E22")}),1.0]])]});
            var Q1;
            Q1=makeQuery(id+"F6.imprint","IMPRINT",FACE,{"disambiguationData":[TD([[makeQuery(id+"F6.imprint","IMPRINT",EDGE,{"derivedFrom":sQuery(id+"F6.wireOp",EDGE,"E23")}),1.0]])]});
            var Q2;
            Q2=makeQuery(id+"F6.imprint","IMPRINT",FACE,{"disambiguationData":[TD([[makeQuery(id+"F6.imprint","IMPRINT",EDGE,{"derivedFrom":sQuery(id+"F6.wireOp",EDGE,"E24")}),1.0]])]});
            var Q3;
            Q3=makeQuery(id+"F6.imprint","IMPRINT",FACE,{"disambiguationData":[TD([[makeQuery(id+"F6.imprint","IMPRINT",EDGE,{"derivedFrom":sQuery(id+"F6.wireOp",EDGE,"E25")}),1.0]])]});
            extrude(context, id + "F7", {"entities" : qUnion([Q0, Q1, Q2, Q3]), "operationType" : NewBodyOperationType.REMOVE, "endBound" : BoundingType.THROUGH_ALL, "oppositeDirection" : true, "depth" : 25 * mm, "offsetDistance" : 25 * mm});
        }
        {
            var Q0;
            Q0=makeQuery(id+"F1.opExtrude","CAP_FACE",FACE,{"disambiguationData":[OSD([sQuery(id+"F0.wireOp",EDGE,"E0.bottom"),sQuery(id+"F0.wireOp",EDGE,"E0.top"),sQuery(id+"F0.wireOp",EDGE,"E0.left"),sQuery(id+"F0.wireOp",EDGE,"E0.right"),sQuery(id+"F0.wireOp",EDGE,"E1.filletArc"),sQuery(id+"F0.wireOp",EDGE,"E2.filletArc"),sQuery(id+"F0.wireOp",EDGE,"E3.filletArc"),sQuery(id+"F0.wireOp",EDGE,"E4.filletArc")])],"isStart":false});
            shell(context, id + "F8", {"entities" : qUnion([Q0]), "thickness" : 2 * mm});
        }
        {
            var Q0;
            Q0=makeQuery(id+"F7.boolean.opBoolean","INTERSECT",EDGE,{"derivedFrom":[makeQuery(id+"F1.opExtrude","CAP_FACE",FACE,{"disambiguationData":[OSD([sQuery(id+"F0.wireOp",EDGE,"E0.bottom"),sQuery(id+"F0.wireOp",EDGE,"E0.top"),sQuery(id+"F0.wireOp",EDGE,"E0.left"),sQuery(id+"F0.wireOp",EDGE,"E0.right"),sQuery(id+"F0.wireOp",EDGE,"E1.filletArc"),sQuery(id+"F0.wireOp",EDGE,"E2.filletArc"),sQuery(id+"F0.wireOp",EDGE,"E3.filletArc"),sQuery(id+"F0.wireOp",EDGE,"E4.filletArc")])],"isStart":true}),makeQuery(id+"F7.opExtrude","SWEPT_FACE",FACE,{"disambiguationData":[OSD([sQuery(id+"F6.wireOp",EDGE,"E23")])]})]});
            var Q1;
            Q1=makeQuery(id+"F7.boolean.opBoolean","INTERSECT",EDGE,{"derivedFrom":[makeQuery(id+"F1.opExtrude","CAP_FACE",FACE,{"disambiguationData":[OSD([sQuery(id+"F0.wireOp",EDGE,"E0.bottom"),sQuery(id+"F0.wireOp",EDGE,"E0.top"),sQuery(id+"F0.wireOp",EDGE,"E0.left"),sQuery(id+"F0.wireOp",EDGE,"E0.right"),sQuery(id+"F0.wireOp",EDGE,"E1.filletArc"),sQuery(id+"F0.wireOp",EDGE,"E2.filletArc"),sQuery(id+"F0.wireOp",EDGE,"E3.filletArc"),sQuery(id+"F0.wireOp",EDGE,"E4.filletArc")])],"isStart":true}),makeQuery(id+"F7.opExtrude","SWEPT_FACE",FACE,{"disambiguationData":[OSD([sQuery(id+"F6.wireOp",EDGE,"E22")])]})]});
            var Q2;
            Q2=makeQuery(id+"F7.boolean.opBoolean","INTERSECT",EDGE,{"derivedFrom":[makeQuery(id+"F1.opExtrude","CAP_FACE",FACE,{"disambiguationData":[OSD([sQuery(id+"F0.wireOp",EDGE,"E0.bottom"),sQuery(id+"F0.wireOp",EDGE,"E0.top"),sQuery(id+"F0.wireOp",EDGE,"E0.left"),sQuery(id+"F0.wireOp",EDGE,"E0.right"),sQuery(id+"F0.wireOp",EDGE,"E1.filletArc"),sQuery(id+"F0.wireOp",EDGE,"E2.filletArc"),sQuery(id+"F0.wireOp",EDGE,"E3.filletArc"),sQuery(id+"F0.wireOp",EDGE,"E4.filletArc")])],"isStart":true}),makeQuery(id+"F7.opExtrude","SWEPT_FACE",FACE,{"disambiguationData":[OSD([sQuery(id+"F6.wireOp",EDGE,"E25")])]})]});
            var Q3;
            Q3=makeQuery(id+"F7.boolean.opBoolean","INTERSECT",EDGE,{"derivedFrom":[makeQuery(id+"F1.opExtrude","CAP_FACE",FACE,{"disambiguationData":[OSD([sQuery(id+"F0.wireOp",EDGE,"E0.bottom"),sQuery(id+"F0.wireOp",EDGE,"E0.top"),sQuery(id+"F0.wireOp",EDGE,"E0.left"),sQuery(id+"F0.wireOp",EDGE,"E0.right"),sQuery(id+"F0.wireOp",EDGE,"E1.filletArc"),sQuery(id+"F0.wireOp",EDGE,"E2.filletArc"),sQuery(id+"F0.wireOp",EDGE,"E3.filletArc"),sQuery(id+"F0.wireOp",EDGE,"E4.filletArc")])],"isStart":true}),makeQuery(id+"F7.opExtrude","SWEPT_FACE",FACE,{"disambiguationData":[OSD([sQuery(id+"F6.wireOp",EDGE,"E24")])]})]});
            chamfer(context, id + "F9", {"entities" : qUnion([Q0, Q1, Q2, Q3]), "chamferType" : ChamferType.OFFSET_ANGLE, "width" : 2 * mm, "oppositeDirection" : false, "angle" : 45 * degree, "tangentPropagation" : true});
        }
        {
            var Q0;
            Q0=makeQuery(id+"F1.opExtrude","CAP_FACE",FACE,{"disambiguationData":[OSD([sQuery(id+"F0.wireOp",EDGE,"E0.bottom"),sQuery(id+"F0.wireOp",EDGE,"E0.top"),sQuery(id+"F0.wireOp",EDGE,"E0.left"),sQuery(id+"F0.wireOp",EDGE,"E0.right"),sQuery(id+"F0.wireOp",EDGE,"E1.filletArc"),sQuery(id+"F0.wireOp",EDGE,"E2.filletArc"),sQuery(id+"F0.wireOp",EDGE,"E3.filletArc"),sQuery(id+"F0.wireOp",EDGE,"E4.filletArc")])],"isStart":false});
            var sketch = newSketch(context, id + "F10", { "sketchPlane" : qUnion([Q0])});
            skLineSegment(sketch, "E26.0", {"start": v(17.5, 26.5) * mm, "end": v(-17.5, 26.5) * mm});
            skArc(sketch, "E26.1", {"start": v(26.5, 17.5) * mm, "mid": v(23.86, 23.86) * mm, "end": v(17.5, 26.5) * mm});
            skArc(sketch, "E26.2", {"start": v(-17.5, 26.5) * mm, "mid": v(-23.86, 23.86) * mm, "end": v(-26.5, 17.5) * mm});
            skLineSegment(sketch, "E26.3", {"start": v(26.5, -17.5) * mm, "end": v(26.5, 17.5) * mm});
            skLineSegment(sketch, "E26.4", {"start": v(-26.5, -17.5) * mm, "end": v(-26.5, 17.5) * mm});
            skArc(sketch, "E26.5", {"start": v(-26.5, -17.5) * mm, "mid": v(-23.86, -23.86) * mm, "end": v(-17.5, -26.5) * mm});
            skLineSegment(sketch, "E26.6", {"start": v(17.5, -26.5) * mm, "end": v(-17.5, -26.5) * mm});
            skArc(sketch, "E26.7", {"start": v(17.5, -26.5) * mm, "mid": v(23.86, -23.86) * mm, "end": v(26.5, -17.5) * mm});
            skSolve(sketch);
        }
        {
            var Q0;
            Q0=makeQuery(id+"F10.imprint","IMPRINT",FACE,{"disambiguationData":[TD([[makeQuery(id+"F10.imprint","IMPRINT",EDGE,{"derivedFrom":sQuery(id+"F10.wireOp",EDGE,"E26.0")}),-1.0]])]});
            extrude(context, id + "F11", {"entities" : qUnion([Q0]), "operationType" : NewBodyOperationType.REMOVE, "oppositeDirection" : true, "depth" : 2 * mm, "offsetDistance" : 25 * mm});
        }
    });
